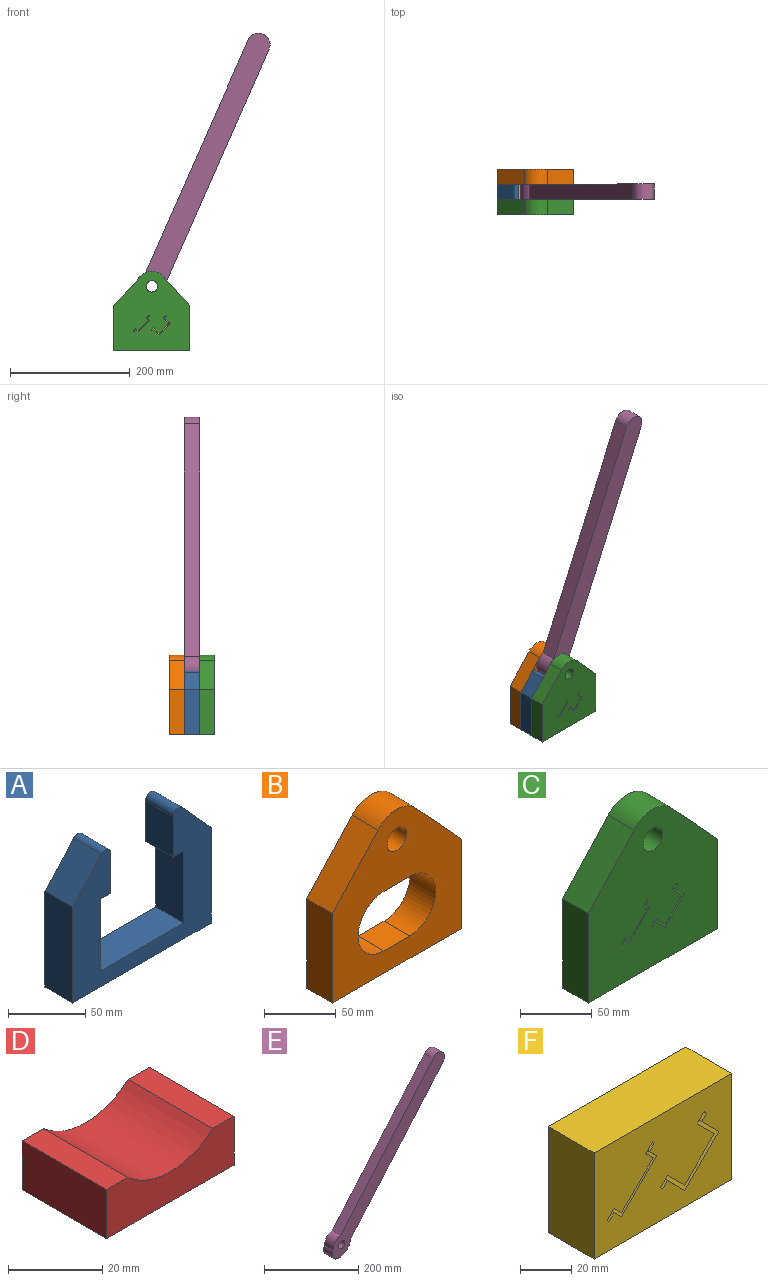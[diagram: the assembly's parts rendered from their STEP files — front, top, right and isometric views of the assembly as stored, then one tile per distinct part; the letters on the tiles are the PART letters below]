
ASSEMBLY  parts=6 mates=6
PART A: 16 faces, bbox 127x25.4x106.7 mm
  f0: plane 76.45x25.4mm, normal (0,0,1), area 1941.9mm2, adj f1,f9,f10,f11
  f1: plane 57.15x25.4mm, normal (1,0,0), area 1451.6mm2, adj f0,f2,f10,f11
  f2: plane 25.4x9.53mm, normal (0,0,-1), area 241.9mm2, adj f1,f3,f10,f11
  f3: plane 32.11x25.4mm, normal (1,0,0), area 815.5mm2, adj f2,f10,f11,f14
  f4: plane 76.2x25.4mm, normal (-1,0,0), area 1935.5mm2, adj f5,f10,f11,f15
  f5: plane 127x25.4mm, normal (0,0,-1), area 3225.8mm2, adj f4,f6,f10,f11
  f6: plane 76.2x25.4mm, normal (1,0,0), area 1935.5mm2, adj f5,f10,f11,f12
  f7: plane 32.11x25.4mm, normal (-1,0,0), area 815.5mm2, adj f8,f10,f11,f13
  f8: plane 25.4x9.53mm, normal (0,0,-1), area 241.9mm2, adj f7,f9,f10,f11
  f9: plane 57.15x25.4mm, normal (-1,0,0), area 1451.6mm2, adj f0,f8,f10,f11
  f10: plane 127x106.72mm, normal (0,-1,0), area 6204mm2, adj f0,f1,f2,f3,f4,f5,f6,f7
  f11: plane 127x106.72mm, normal (0,1,0), area 6204mm2, adj f0,f1,f2,f3,f4,f5,f6,f7
  f12: plane 28.97x26.52mm, normal (0.74,0,0.68), area 997.7mm2, adj f6,f10,f11,f13
  f13: cylinder r=4.76mm len=25.4mm, axis (0,1,0), area 290.4mm2, adj f7,f10,f11,f12
  f14: cylinder r=4.76mm len=25.4mm, axis (0,1,0), area 290.4mm2, adj f3,f10,f11,f15
  f15: plane 28.97x26.52mm, normal (-0.74,0,0.68), area 997.7mm2, adj f4,f10,f11,f14
PART B: 13 faces, bbox 127x25.4x133.4 mm
  f0: plane 76.2x25.4mm, normal (1,0,0), area 1935.5mm2, adj f1,f5,f7,f8
  f1: plane 48.9x44.76mm, normal (0.74,0,0.68), area 1683.9mm2, adj f0,f2,f7,f8
  f2: cylinder r=25.4mm len=37.47mm, axis (0,-1,0), area 1070.4mm2, adj f1,f3,f7,f8
  f3: plane 48.9x44.76mm, normal (-0.74,0,0.68), area 1683.9mm2, adj f2,f4,f7,f8
  f4: plane 76.2x25.4mm, normal (-1,0,0), area 1935.5mm2, adj f3,f5,f7,f8
  f5: plane 127x25.4mm, normal (0,0,-1), area 3225.8mm2, adj f0,f4,f7,f8
  f6: cylinder r=9.53mm len=25.4mm, axis (0,-1,0), area 1520.1mm2, adj f7,f8
  f7: plane 133.35x127mm, normal (0,1,0), area 10310.4mm2, adj f0,f1,f2,f3,f4,f5,f6,f9
  f8: plane 133.35x127mm, normal (0,-1,0), area 10310.4mm2, adj f0,f1,f2,f3,f4,f5,f6,f9
  f9: plane 25.4x25.4mm, normal (0,0,-1), area 645.2mm2, adj f7,f8,f10,f12
  f10: cylinder r=25.4mm len=50.8mm, axis (0,1,0), area 2026.8mm2, adj f7,f8,f9,f11
  f11: plane 25.4x25.4mm, normal (0,0,1), area 645.2mm2, adj f7,f8,f10,f12
  f12: cylinder r=25.4mm len=50.8mm, axis (0,1,0), area 2026.8mm2, adj f7,f8,f9,f11
PART C: 41 faces, bbox 127x25.4x133.4 mm
  f0: plane 133.35x127mm, normal (0,-1,0), area 13454.1mm2, adj f2,f3,f4,f5,f6,f7,f8,f9
  f1: plane 133.35x127mm, normal (0,1,0), area 13454.1mm2, adj f2,f3,f4,f5,f6,f7,f8,f9
  f2: plane 76.2x25.4mm, normal (1,0,0), area 1935.5mm2, adj f0,f1,f3,f7
  f3: plane 48.9x44.76mm, normal (0.74,0,0.68), area 1683.9mm2, adj f0,f1,f2,f4
  f4: cylinder r=25.4mm len=37.47mm, axis (0,1,0), area 1070.4mm2, adj f0,f1,f3,f5
  f5: plane 48.9x44.76mm, normal (-0.74,0,0.68), area 1683.9mm2, adj f0,f1,f4,f6
  f6: plane 76.2x25.4mm, normal (-1,0,0), area 1935.5mm2, adj f0,f1,f5,f7
  f7: plane 127x25.4mm, normal (0,0,-1), area 3225.8mm2, adj f0,f1,f2,f6
  f8: cylinder r=9.53mm len=25.4mm, axis (0,1,0), area 1520.1mm2, adj f0,f1
  f9: plane 25.4x3.5mm, normal (0.71,0,-0.71), area 125.8mm2, adj f0,f1,f20,f33
  f10: plane 25.4x0.27mm, normal (0.71,0,0.71), area 9.7mm2, adj f0,f1,f33,f34
  f11: plane 25.4x2.51mm, normal (-0.71,0,0.71), area 90.3mm2, adj f0,f1,f12,f34
  f12: plane 25.4x4.04mm, normal (0.71,0,0.71), area 145.2mm2, adj f0,f1,f11,f13
  f13: plane 25.4x19.54mm, normal (-0.71,0,0.71), area 701.9mm2, adj f0,f1,f12,f14
  f14: plane 25.4x4.04mm, normal (-0.71,0,-0.71), area 145.2mm2, adj f0,f1,f13,f15
  f15: plane 25.4x2.51mm, normal (-0.71,0,0.71), area 90.3mm2, adj f0,f1,f14,f35
  f16: plane 25.4x0.27mm, normal (-0.71,0,-0.71), area 9.7mm2, adj f0,f1,f35,f36
  f17: plane 25.4x3.5mm, normal (0.71,0,-0.71), area 125.8mm2, adj f0,f1,f18,f36
  f18: plane 25.4x4.04mm, normal (0.71,0,0.71), area 145.2mm2, adj f0,f1,f17,f19
  f19: plane 25.4x17.57mm, normal (0.71,0,-0.71), area 631mm2, adj f0,f1,f18,f20
  f20: plane 25.4x4.04mm, normal (-0.71,0,-0.71), area 145.2mm2, adj f0,f1,f9,f19
  f21: plane 25.4x18.9mm, normal (-0.71,0,0.71), area 679mm2, adj f0,f1,f22,f32
  f22: plane 25.4x9.43mm, normal (-0.71,0,-0.71), area 338.7mm2, adj f0,f1,f21,f23
  f23: plane 25.4x2.25mm, normal (-0.71,0,0.71), area 80.6mm2, adj f0,f1,f22,f40
  f24: plane 25.4x0.54mm, normal (-0.71,0,-0.71), area 19.4mm2, adj f0,f1,f39,f40
  f25: plane 25.4x3.5mm, normal (0.71,0,-0.71), area 125.8mm2, adj f0,f1,f26,f39
  f26: plane 25.4x9.43mm, normal (0.71,0,0.71), area 338.7mm2, adj f0,f1,f25,f27
  f27: plane 25.4x16.39mm, normal (0.71,0,-0.71), area 588.7mm2, adj f0,f1,f26,f28
  f28: plane 25.4x9.43mm, normal (-0.71,0,-0.71), area 338.7mm2, adj f0,f1,f27,f29
  f29: plane 25.4x3.5mm, normal (0.71,0,-0.71), area 125.8mm2, adj f0,f1,f28,f38
  f30: plane 25.4x0.54mm, normal (0.71,0,0.71), area 19.4mm2, adj f0,f1,f37,f38
  f31: plane 25.4x2.25mm, normal (-0.71,0,0.71), area 80.6mm2, adj f0,f1,f32,f37
  f32: plane 25.4x9.43mm, normal (0.71,0,0.71), area 338.7mm2, adj f0,f1,f21,f31
  f33: cylinder r=0.51mm len=25.4mm, axis (0,1,0), area 20.3mm2, adj f0,f1,f9,f10
  f34: cylinder r=0.51mm len=25.4mm, axis (0,-1,0), area 20.3mm2, adj f0,f1,f10,f11
  f35: cylinder r=0.51mm len=25.4mm, axis (0,1,0), area 20.3mm2, adj f0,f1,f15,f16
  f36: cylinder r=0.51mm len=25.4mm, axis (0,-1,0), area 20.3mm2, adj f0,f1,f16,f17
  f37: cylinder r=0.51mm len=25.4mm, axis (0,-1,0), area 20.3mm2, adj f0,f1,f30,f31
  f38: cylinder r=0.51mm len=25.4mm, axis (0,1,0), area 20.3mm2, adj f0,f1,f29,f30
  f39: cylinder r=0.51mm len=25.4mm, axis (0,-1,0), area 20.3mm2, adj f0,f1,f24,f25
  f40: cylinder r=0.51mm len=25.4mm, axis (0,1,0), area 20.3mm2, adj f0,f1,f23,f24
PART D: 8 faces, bbox 38.1x25.4x12.7 mm
  f0: plane 25.4x12.7mm, normal (-1,0,0), area 322.6mm2, adj f1,f5,f6,f7
  f1: plane 38.1x25.4mm, normal (0,0,-1), area 967.7mm2, adj f0,f2,f6,f7
  f2: plane 25.4x12.7mm, normal (1,0,0), area 322.6mm2, adj f1,f3,f6,f7
  f3: plane 25.4x6.35mm, normal (0,0,1), area 161.3mm2, adj f2,f4,f6,f7
  f4: cylinder r=19.05mm len=25.4mm, axis (0,1,0), area 706.2mm2, adj f3,f5,f6,f7
  f5: plane 25.4x6.35mm, normal (0,0,1), area 161.3mm2, adj f0,f4,f6,f7
  f6: plane 38.1x12.7mm, normal (0,-1,0), area 399.4mm2, adj f0,f1,f2,f3,f4,f5
  f7: plane 38.1x12.7mm, normal (0,1,0), area 399.4mm2, adj f0,f1,f2,f3,f4,f5
PART E: 9 faces, bbox 336.6x25.4x384.4 mm
  f0: cylinder r=19.05mm len=31.73mm, axis (0,1,0), area 1393mm2, adj f1,f5,f7,f8
  f1: cylinder r=24.24mm len=25.95mm, axis (0,1,0), area 971.5mm2, adj f0,f2,f7,f8
  f2: plane 322.18x277.63mm, normal (0.76,0,-0.65), area 10802.5mm2, adj f1,f3,f7,f8
  f3: cylinder r=19.05mm len=33.48mm, axis (0,1,0), area 1520.1mm2, adj f2,f4,f7,f8
  f4: plane 322.18x277.63mm, normal (-0.76,0,0.65), area 10802.5mm2, adj f3,f5,f7,f8
  f5: cylinder r=24.24mm len=26.17mm, axis (0,1,0), area 971.5mm2, adj f0,f4,f7,f8
  f6: cylinder r=9.53mm len=25.4mm, axis (0,1,0), area 1520.1mm2, adj f7,f8
  f7: plane 384.45x336.55mm, normal (0,-1,0), area 18608.6mm2, adj f0,f1,f2,f3,f4,f5,f6
  f8: plane 384.45x336.55mm, normal (0,1,0), area 18608.6mm2, adj f0,f1,f2,f3,f4,f5,f6
PART F: 30 faces, bbox 76.2x25.4x50.8 mm
  f0: plane 25.4x0.99mm, normal (0.71,0,0.71), area 35.5mm2, adj f1,f27,f28,f29
  f1: plane 25.4x3.86mm, normal (0.71,0,-0.71), area 138.7mm2, adj f0,f2,f28,f29
  f2: plane 25.4x4.04mm, normal (-0.71,0,-0.71), area 145.2mm2, adj f1,f3,f28,f29
  f3: plane 25.4x17.57mm, normal (0.71,0,-0.71), area 631mm2, adj f2,f4,f28,f29
  f4: plane 25.4x4.04mm, normal (0.71,0,0.71), area 145.2mm2, adj f3,f5,f28,f29
  f5: plane 25.4x3.86mm, normal (0.71,0,-0.71), area 138.7mm2, adj f4,f6,f28,f29
  f6: plane 25.4x0.99mm, normal (-0.71,0,-0.71), area 35.5mm2, adj f5,f7,f28,f29
  f7: plane 25.4x2.87mm, normal (-0.71,0,0.71), area 103.2mm2, adj f6,f8,f28,f29
  f8: plane 25.4x4.04mm, normal (-0.71,0,-0.71), area 145.2mm2, adj f7,f9,f28,f29
  f9: plane 25.4x19.54mm, normal (-0.71,0,0.71), area 701.9mm2, adj f8,f10,f28,f29
  f10: plane 25.4x4.04mm, normal (0.71,0,0.71), area 145.2mm2, adj f9,f27,f28,f29
  f11: plane 25.4x9.43mm, normal (-0.71,0,-0.71), area 338.7mm2, adj f12,f25,f28,f29
  f12: plane 25.4x18.9mm, normal (-0.71,0,0.71), area 679mm2, adj f11,f13,f28,f29
  f13: plane 25.4x9.43mm, normal (0.71,0,0.71), area 338.7mm2, adj f12,f14,f28,f29
  f14: plane 25.4x2.6mm, normal (-0.71,0,0.71), area 93.5mm2, adj f13,f15,f28,f29
  f15: plane 25.4x1.26mm, normal (0.71,0,0.71), area 45.2mm2, adj f14,f16,f28,f29
  f16: plane 25.4x3.86mm, normal (0.71,0,-0.71), area 138.7mm2, adj f15,f17,f28,f29
  f17: plane 25.4x9.43mm, normal (-0.71,0,-0.71), area 338.7mm2, adj f16,f18,f28,f29
  f18: plane 25.4x16.39mm, normal (0.71,0,-0.71), area 588.7mm2, adj f17,f19,f28,f29
  f19: plane 25.4x9.43mm, normal (0.71,0,0.71), area 338.7mm2, adj f18,f20,f28,f29
  f20: plane 25.4x3.86mm, normal (0.71,0,-0.71), area 138.7mm2, adj f19,f21,f28,f29
  f21: plane 25.4x1.26mm, normal (-0.71,0,-0.71), area 45.2mm2, adj f20,f25,f28,f29
  f22: plane 50.8x25.4mm, normal (1,0,0), area 1290.3mm2, adj f23,f26,f28,f29
  f23: plane 76.2x25.4mm, normal (0,0,1), area 1935.5mm2, adj f22,f24,f28,f29
  f24: plane 50.8x25.4mm, normal (-1,0,0), area 1290.3mm2, adj f23,f26,f28,f29
  f25: plane 25.4x2.6mm, normal (-0.71,0,0.71), area 93.5mm2, adj f11,f21,f28,f29
  f26: plane 76.2x25.4mm, normal (0,0,-1), area 1935.5mm2, adj f22,f24,f28,f29
  f27: plane 25.4x2.87mm, normal (-0.71,0,0.71), area 103.2mm2, adj f0,f10,f28,f29
  f28: plane 76.2x50.8mm, normal (0,-1,0), area 3697mm2, adj f0,f1,f2,f3,f4,f5,f6,f7
  f29: plane 76.2x50.8mm, normal (0,1,0), area 3697mm2, adj f0,f1,f2,f3,f4,f5,f6,f7
PLACE A at identity fixed
PLACE B at identity fixed
PLACE C at identity
PLACE D rot(axis=(-0.02,-0.98,0.2),0deg) t=(3.68,0,-2.33)mm
PLACE E rot(axis=(0,-1,0),16.9deg) t=(18.51,0,2.76)mm
PLACE F rot(axis=(0,-1,0),0deg) t=(-0.13,0,-2.33)mm
MATE planar F.f29 <-> B.f8  axis (0,1,0) through (-0.37,0,-2.19)mm
MATE revolute B.f6 <-> E.f6  axis (0,-1,0) through (0,0,63.5)mm
MATE planar F.f23 <-> D.f1  axis (0,0,1) through (-0.13,-12.7,23.07)mm
MATE fastened C.f7 <-> A.f5  axis (0,0,1) through (63.5,-25.4,-44.45)mm
MATE planar F.f24 <-> A.f1  axis (-1,0,0) through (-38.23,-12.7,-2.33)mm
MATE revolute E.f0 <-> D.f4  axis (0,-1,0) through (-5.97,-25.4,49.97)mm
